# Revit family: MR_ОсветительныйПрибор_FrattoQ
name_source: partatom
category: Осветительные приборы
units: mm (PartAtom-declared; Revit-internal decimal feet)

## family parameters
Всегда вертикально = Да
Источник света = Да
На основе рабочей плоскости = Да
Общий = Да
При загрузке вырезать с полостями = Нет
Размер круглого соединителя = Использовать диаметр
Тип детали = Нормальный
Точка расчета площади = Нет

## types (4) — shared parameters
ADSK_URL страницы изделия = https://martinirus.ru
ADSK_Группирование = Наружное освещение_светильник
ADSK_Единица измерения = шт.
ADSK_Завод-изготовитель = MartiniRUS
ADSK_Классификация нагрузок = Освещение
ADSK_Количество = 1
ADSK_Количество фаз = 1
ADSK_Количество фаз числовое = 1
ADSK_Коэффициент мощности = 0.98
ADSK_Материал = <По категории>
ADSK_Напряжение = 230 В
ADSK_Номинальная мощность = 9 Вт
ADSK_Полная мощность = 9 В·А
ADSK_Ток = 0 А
IP Class = IP65
Видимая форма излучения при визуализации = Да
Группа модели = FRATTO Q
Закладная Тип5_370x370x400 = Нет
Излучение по диаметру окружности = 100 мм
Класс Защиты = I
Описание = FRATTO Q
Отметка по умолчанию = 1219 мм
Полная установленная мощность = 9 В·А
Самосветящий материал = Источник света по умолчанию
Светофильтр = 16777215
Смещение цветовой температуры при затухании лампы = <Нет>
Угол наклона = 90.00°
Файл фотометрической сетки = 1237148_HIT_CE_G12_20150210.IES

## per-type parameters (varying)
| type | ADSK_Код изделия | ADSK_Масса | ADSK_Размер_Высота | Закладная Тип1_H250mm | Закладная Тип1_H500mm |
| FrattoQ_800mm_9w_2700K | P865247__EW | 5.7 | 800 мм | Нет | Да |
| FrattoQ_800mm_9w_4000K | P865247__NW | 5.7 | 800 мм | Нет | Да |
| FrattoQ_350mm_9w_2700K | P865315__EW | 3.8 | 350 мм | Да | Нет |
| FrattoQ_350mm_9w_4000K | P865315__NW | 3.8 | 350 мм | Да | Нет |

note: column(s) folded — value = type name in every type: ADSK_Наименование
